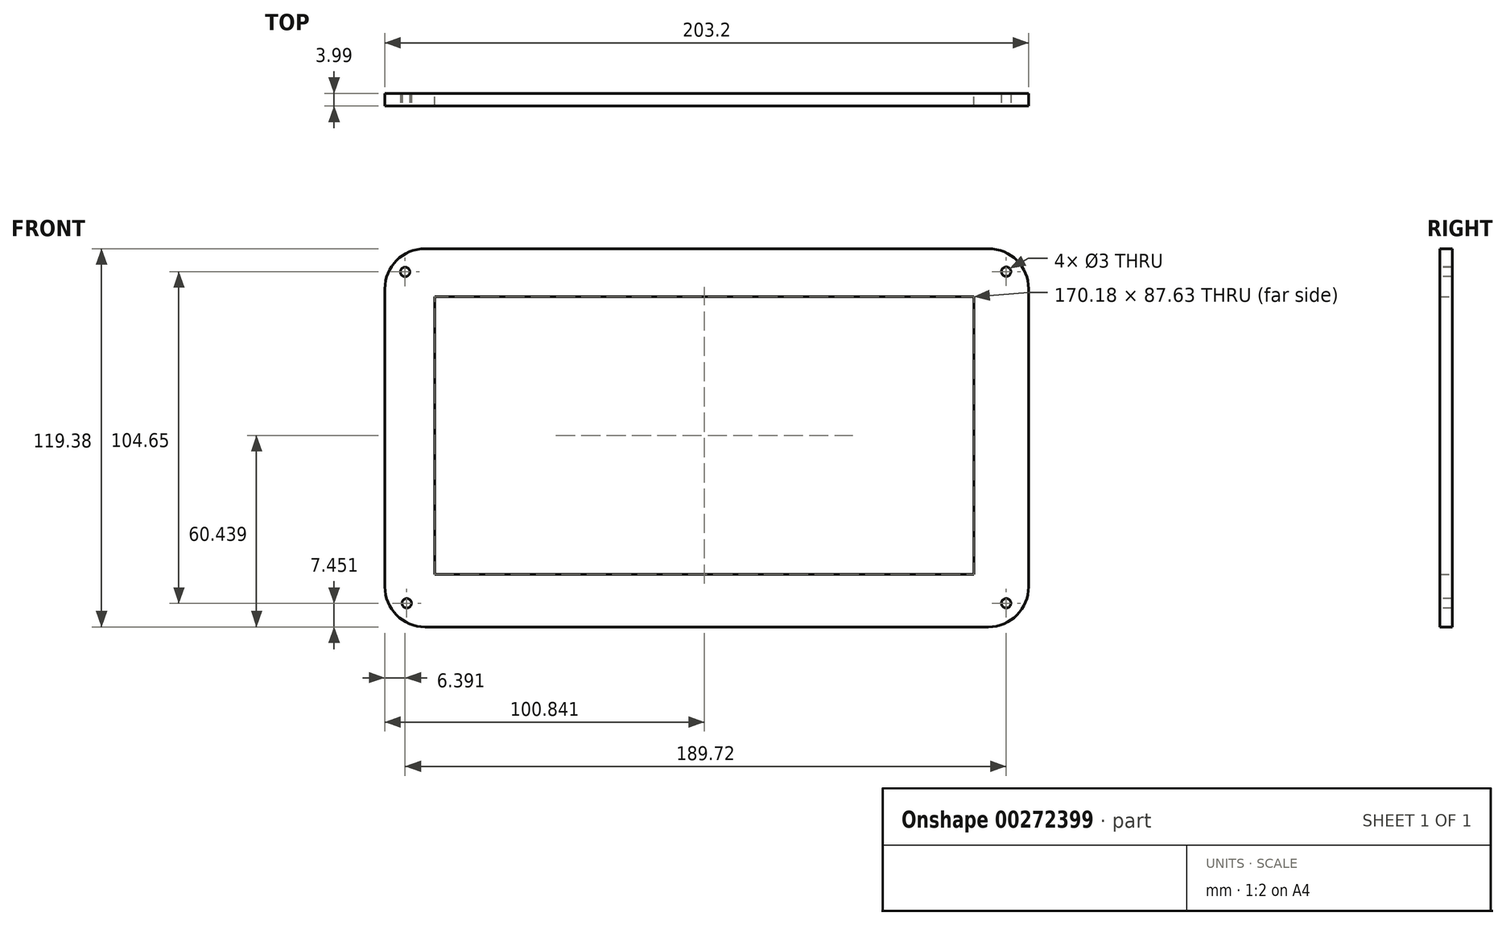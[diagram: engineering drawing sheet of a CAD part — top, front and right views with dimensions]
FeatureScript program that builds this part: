
annotation { "Feature Type Name" : "Feature", "Feature Type Description" : "" }
export const myFeature = defineFeature(function(context is Context, id is Id, definition is map)
    precondition{}
    {
        {
            var Q0;
            Q0=qCreatedBy(makeId("Front.planeOp"),FACE);
            var sketch = newSketch(context, id + "F0", { "sketchPlane" : qUnion([Q0])});
            skLineSegment(sketch, "E0.bottom", {"start": v(-84.6, 50.4) * mm, "end": v(85.58, 50.4) * mm});
            skLineSegment(sketch, "E0.top", {"start": v(-84.6, -37.23) * mm, "end": v(85.58, -37.23) * mm});
            skLineSegment(sketch, "E0.left", {"start": v(-84.6, 50.4) * mm, "end": v(-84.6, -37.23) * mm});
            skLineSegment(sketch, "E0.right", {"start": v(85.58, 50.4) * mm, "end": v(85.58, -37.23) * mm});
            skLineSegment(sketch, "E1.bottom", {"start": v(-87.65, 65.53) * mm, "end": v(90.15, 65.53) * mm});
            skLineSegment(sketch, "E1.top", {"start": v(-87.65, -53.85) * mm, "end": v(90.15, -53.85) * mm});
            skLineSegment(sketch, "E1.left", {"start": v(-100.35, 52.83) * mm, "end": v(-100.35, -41.15) * mm});
            skLineSegment(sketch, "E1.right", {"start": v(102.85, 52.83) * mm, "end": v(102.85, -41.15) * mm});
            skPoint(sketch, "E2.visualSharp", {"position": v(-100.35, 65.53) * mm});
            skArc(sketch, "E2.filletArc", {"start": v(-87.65, 65.53) * mm, "mid": v(-96.63, 61.8) * mm, "end": v(-100.35, 52.83) * mm});
            skPoint(sketch, "E3.visualSharp", {"position": v(-100.35, -53.85) * mm});
            skArc(sketch, "E3.filletArc", {"start": v(-100.35, -41.15) * mm, "mid": v(-96.63, -50.13) * mm, "end": v(-87.65, -53.85) * mm});
            skPoint(sketch, "E4.visualSharp", {"position": v(102.85, -53.85) * mm});
            skArc(sketch, "E4.filletArc", {"start": v(90.15, -53.85) * mm, "mid": v(99.13, -50.13) * mm, "end": v(102.85, -41.15) * mm});
            skPoint(sketch, "E5.visualSharp", {"position": v(102.85, 65.53) * mm});
            skArc(sketch, "E5.filletArc", {"start": v(102.85, 52.83) * mm, "mid": v(99.13, 61.8) * mm, "end": v(90.15, 65.53) * mm});
            skSolve(sketch);
        }
        {
            var Q0;
            Q0=makeQuery(id+"F0.imprint","IMPRINT",FACE,{"disambiguationData":[TD([[makeQuery(id+"F0.imprint","IMPRINT",EDGE,{"derivedFrom":sQuery(id+"F0.wireOp",EDGE,"E0.bottom")}),1.0]])]});
            extrude(context, id + "F1", {"entities" : qUnion([Q0]), "depth" : 4 * mm});
        }
        {
            var Q0;
            Q0=makeQuery(id+"F1.opExtrude","CAP_FACE",FACE,{"disambiguationData":[OSD([sQuery(id+"F0.wireOp",EDGE,"E0.bottom"),sQuery(id+"F0.wireOp",EDGE,"E0.top"),sQuery(id+"F0.wireOp",EDGE,"E0.left"),sQuery(id+"F0.wireOp",EDGE,"E0.right"),sQuery(id+"F0.wireOp",EDGE,"E1.bottom"),sQuery(id+"F0.wireOp",EDGE,"E1.top"),sQuery(id+"F0.wireOp",EDGE,"E1.left"),sQuery(id+"F0.wireOp",EDGE,"E1.right"),sQuery(id+"F0.wireOp",EDGE,"E2.filletArc"),sQuery(id+"F0.wireOp",EDGE,"E3.filletArc"),sQuery(id+"F0.wireOp",EDGE,"E4.filletArc"),sQuery(id+"F0.wireOp",EDGE,"E5.filletArc")])],"isStart":false});
            var sketch = newSketch(context, id + "F2", { "sketchPlane" : qUnion([Q0])});
            skCircle(sketch, "E6", {"center": v(-93.96, 58.2) * mm, "radius": 1.5 * mm});
            skCircle(sketch, "E7", {"center": v(-93.44, -46.4) * mm, "radius": 1.59 * mm});
            skCircle(sketch, "E8", {"center": v(95.76, -46.4) * mm, "radius": 1.7 * mm});
            skCircle(sketch, "E9", {"center": v(95.76, 58.25) * mm, "radius": 1.64 * mm});
            skSolve(sketch);
        }
        {
            var Q0;
            Q0=sQuery(id+"F2.wireOp",VERTEX,"E6.center");
            var Q1;
            Q1=sQuery(id+"F2.wireOp",VERTEX,"E9.center");
            var Q2;
            Q2=sQuery(id+"F2.wireOp",VERTEX,"E8.center");
            var Q3;
            Q3=sQuery(id+"F2.wireOp",VERTEX,"E7.center");
            var Q4;
            Q4=makeQuery(id+"F1.opExtrude","SWEPT_BODY",BODY,{"disambiguationData":[OSD([sQuery(id+"F0.wireOp",EDGE,"E0.bottom"),sQuery(id+"F0.wireOp",EDGE,"E0.top"),sQuery(id+"F0.wireOp",EDGE,"E0.left"),sQuery(id+"F0.wireOp",EDGE,"E0.right"),sQuery(id+"F0.wireOp",EDGE,"E1.bottom"),sQuery(id+"F0.wireOp",EDGE,"E1.top"),sQuery(id+"F0.wireOp",EDGE,"E1.left"),sQuery(id+"F0.wireOp",EDGE,"E1.right"),sQuery(id+"F0.wireOp",EDGE,"E2.filletArc"),sQuery(id+"F0.wireOp",EDGE,"E3.filletArc"),sQuery(id+"F0.wireOp",EDGE,"E4.filletArc"),sQuery(id+"F0.wireOp",EDGE,"E5.filletArc")])]});
            hole(context, id + "F3", {"style" : HoleStyle.SIMPLE, "endStyle" : HoleEndStyle.THROUGH, "holeDiameter" : 3 * mm, "tappedDepth" : 12.7 * mm, "tapClearance" : 3, "locations" : qUnion([Q0, Q1, Q2, Q3]), "scope" : qUnion([Q4])});
        }
    });
